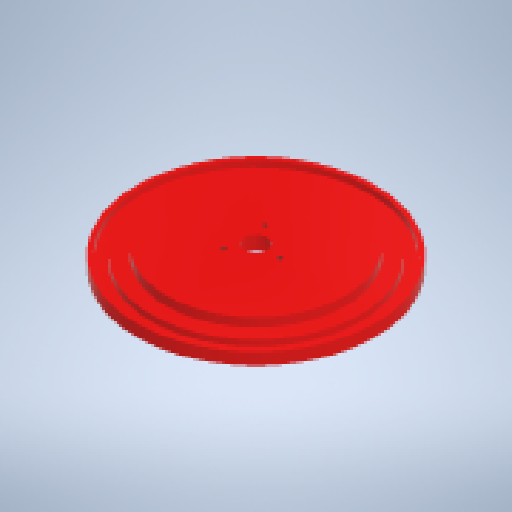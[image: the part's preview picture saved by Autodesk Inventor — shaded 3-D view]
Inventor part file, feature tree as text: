
AUTODESK INVENTOR PART (.ipt)
format: ipt  version: 2023 (Build 270158000, 158)  size: 203,776 bytes
history: native  units: mm
features: revolve x1, hole x1, pattern_circular x1, sketch x1
ambient origin geometry x8: Origin, YZ Plane, XZ Plane, XY Plane, X Axis, Y Axis, Z Axis, Center Point
bodies: Solid1 (feature_tree)
feature tree (4):
  revolve  "Revolution1"  [1 undecoded]
  hole  "Hole1"  [1 undecoded]
  pattern_circular  "Circular Pattern2"  [2 undecoded]
  sketch  "Sketch3"  dims[d0=4.0mm d1=7.0mm d3=80.0mm d4=360.0deg d6=3.5mm d7=2.0mm d15=70.0mm d16=7.0mm d17=1.5mm d18=3.0mm d23=1.567mm d24=4.0mm d25=4.0mm d26=2.0mm d27=90.0deg d28=5.0mm d29=20.594885mm d33=3.0mm d34=60.0mm d35=7.5mm d36=10.0mm d37=30.0mm d38=360.0deg d40=14.0mm d41=2.0mm]
note: 4 required parameter values undecoded (feature->parameter linkage not recoverable at this tier; creation-order binding heuristic only, values carry confidence <= 0.55)